# Revit family: Faucet-Two_Handle-American_Standard-Crawford-7612207_Series
name_source: partatom
category: Plumbing Fixtures
revit_build: Autodesk Revit 2018 (Build: 20170223_1515(x64)
units: mm (PartAtom-declared; Revit-internal decimal feet)

## family parameters
Always vertical = No
Cut with Voids When Loaded = No
OmniClass Number = 23.45.55.17
OmniClass Title = Mixing Faucets
Part Type = Normal
Room Calculation Point = No
Round Connector Dimension = Use Diameter
Shared = Yes
Work Plane-Based = Yes

## types (4) — shared parameters
ADA Compliant = Yes
Assembly Code = D2020300
CW Connection = Yes
CWFU = 1.5
Cold Water Connection Diameter = 3/8"
Compliance Certifications = These products meet or exceed:ANSI A117.1,ASME A112.18.1,CSA B125.1,NSF 61/Section 9,NSF 372
Default Elevation = 0"
Description = Crawford™ 4-Inch Centerset 2-Handle Bathroom Faucet 1.2 gpm/4.5 L/min With Lever Handles
Flow Rate = 1.2 gpm (4.5L/min)
HW Connection = Yes
HWFU = 1.5
Height = 6 3/4"
Hot Water Connection Diameter = 3/8"
Installation Type = Deck Mounted
Length = 8 15/16"
Manufacturer = American Standard
Pop Up Drain = Yes
Pop Up Drain Depth = 3"
Pop Up Drain Width = 5"
Product Documentation Link = https://americanstandard.box.com
Product Page URL = https://www.americanstandard-us.com
URL = http://www.americanstandard-us.com
Vent Connection = No
Warranty Information = Limited Lifetime Warranty
Waste Connection = No
Width = 6 1/4"
zero-valued in all types: WFU

## per-type parameters (varying)
| type | Finish | Material |
| 7612207.002 | Metal-American Standard-002-Polished Chrome | Metal-American Standard-002-Polished Chrome |
| 7612207.295 | Metal-American Standard-295-Brushed Nickel | Metal-American Standard-295-Brushed Nickel |
| 7612207.243 | Metal-American Standard-243-Matte Black | Metal-American Standard-243-Matte Black |
| 7612207.278 | Metal-American Standard-278-Legacy Bronze | Metal-American Standard-278-Legacy Bronze |

note: column(s) folded — value = type name in every type: Model

## geometry (parser evidence)
native form markers: Sweep x2
no freeform markers — native parametric forms only
